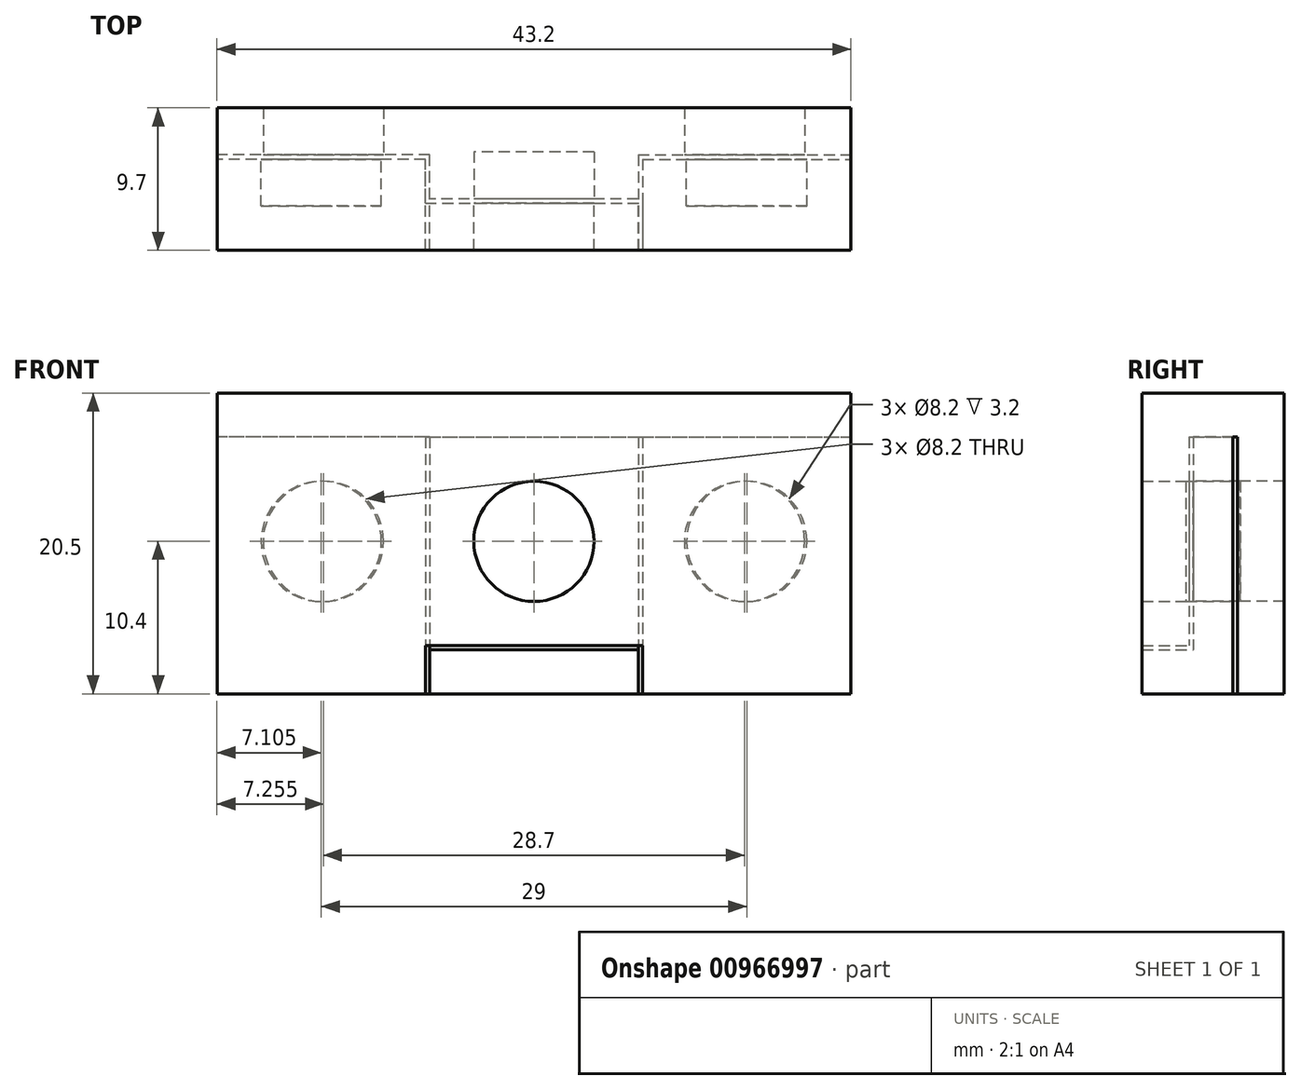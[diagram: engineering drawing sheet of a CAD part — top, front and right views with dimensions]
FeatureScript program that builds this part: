
annotation { "Feature Type Name" : "Feature", "Feature Type Description" : "" }
export const myFeature = defineFeature(function(context is Context, id is Id, definition is map)
    precondition{}
    {
        {
            var Q0;
            Q0=qCreatedBy(makeId("Top.planeOp"),FACE);
            var sketch = newSketch(context, id + "F0", { "sketchPlane" : qUnion([Q0])});
            skLineSegment(sketch, "E0.bottom", {"start": v(-40.9, 15.59) * mm, "end": v(2.3, 15.59) * mm});
            skLineSegment(sketch, "E0.top", {"start": v(-40.9, 25.29) * mm, "end": v(2.3, 25.29) * mm});
            skLineSegment(sketch, "E1", {"start": v(-26.7, 18.79) * mm, "end": v(-11.9, 18.79) * mm});
            skLineSegment(sketch, "E2", {"start": v(-26.7, 21.79) * mm, "end": v(-40.9, 21.79) * mm});
            skLineSegment(sketch, "E3", {"start": v(-11.9, 21.79) * mm, "end": v(2.3, 21.79) * mm});
            skLineSegment(sketch, "E4", {"start": v(-11.9, 21.79) * mm, "end": v(-11.9, 18.79) * mm});
            skLineSegment(sketch, "E5", {"start": v(-26.7, 18.79) * mm, "end": v(-26.7, 21.79) * mm});
            skLineSegment(sketch, "E6.0", {"start": v(-12.2, 22.09) * mm, "end": v(2.3, 22.09) * mm});
            skLineSegment(sketch, "E6.1", {"start": v(-26.4, 22.09) * mm, "end": v(-40.9, 22.09) * mm});
            skLineSegment(sketch, "E6.2", {"start": v(-26.4, 19.09) * mm, "end": v(-26.4, 22.09) * mm});
            skLineSegment(sketch, "E6.3", {"start": v(-26.4, 19.09) * mm, "end": v(-12.2, 19.09) * mm});
            skLineSegment(sketch, "E6.4", {"start": v(-12.2, 22.09) * mm, "end": v(-12.2, 19.09) * mm});
            skLineSegment(sketch, "E7", {"start": v(-40.9, 15.59) * mm, "end": v(-40.9, 21.79) * mm});
            skLineSegment(sketch, "E8", {"start": v(2.3, 15.59) * mm, "end": v(2.3, 21.79) * mm});
            skLineSegment(sketch, "E9", {"start": v(2.3, 22.09) * mm, "end": v(2.3, 25.29) * mm});
            skLineSegment(sketch, "E10", {"start": v(-40.9, 22.09) * mm, "end": v(-40.9, 25.29) * mm});
            skSolve(sketch);
        }
        {
            var Q0;
            Q0=makeQuery(id+"F0.imprint","IMPRINT",FACE,{"disambiguationData":[TD([[makeQuery(id+"F0.imprint","IMPRINT",EDGE,{"derivedFrom":sQuery(id+"F0.wireOp",EDGE,"E0.bottom")}),1.0]])]});
            extrude(context, id + "F1", {"entities" : qUnion([Q0]), "depth" : 14.2 * mm, "offsetDistance" : 25 * mm});
        }
        {
            var Q0;
            Q0=makeQuery(id+"F0.imprint","IMPRINT",FACE,{"disambiguationData":[TD([[makeQuery(id+"F0.imprint","IMPRINT",EDGE,{"derivedFrom":sQuery(id+"F0.wireOp",EDGE,"E0.top")}),-1.0]])]});
            extrude(context, id + "F2", {"entities" : qUnion([Q0]), "depth" : 14.2 * mm, "offsetDistance" : 25 * mm});
        }
        {
            var Q0;
            Q0=makeQuery(id+"F1.opExtrude","SWEPT_FACE",FACE,{"disambiguationData":[OSD([sQuery(id+"F0.wireOp",EDGE,"E2")])]});
            var sketch = newSketch(context, id + "F3", { "sketchPlane" : qUnion([Q0])});
            skCircle(sketch, "E11", {"center": v(33.8, 7.1) * mm, "radius": 4.1 * mm});
            skSolve(sketch);
        }
        {
            var Q0;
            Q0=makeQuery(id+"F1.opExtrude","SWEPT_FACE",FACE,{"disambiguationData":[OSD([sQuery(id+"F0.wireOp",EDGE,"E3")])]});
            var sketch = newSketch(context, id + "F4", { "sketchPlane" : qUnion([Q0])});
            skCircle(sketch, "E12", {"center": v(4.8, 7.1) * mm, "radius": 4.1 * mm});
            skSolve(sketch);
        }
        {
            var Q0;
            Q0=makeQuery(id+"F4.imprint","IMPRINT",FACE,{"disambiguationData":[TD([[makeQuery(id+"F4.imprint","IMPRINT",EDGE,{"derivedFrom":sQuery(id+"F4.wireOp",EDGE,"E12")}),1.0]])]});
            var Q1;
            Q1=makeQuery(id+"F3.imprint","IMPRINT",FACE,{"disambiguationData":[TD([[makeQuery(id+"F3.imprint","IMPRINT",EDGE,{"derivedFrom":sQuery(id+"F3.wireOp",EDGE,"E11")}),1.0]])]});
            extrude(context, id + "F5", {"entities" : qUnion([Q0, Q1]), "operationType" : NewBodyOperationType.REMOVE, "oppositeDirection" : true, "depth" : 3.2 * mm, "offsetDistance" : 25 * mm});
        }
        {
            var Q0;
            Q0=makeQuery(id+"F1.opExtrude","SWEPT_FACE",FACE,{"disambiguationData":[OSD([sQuery(id+"F0.wireOp",EDGE,"E1")])]});
            var sketch = newSketch(context, id + "F6", { "sketchPlane" : qUnion([Q0])});
            skCircle(sketch, "E13", {"center": v(19.3, 7.1) * mm, "radius": 4.1 * mm});
            skLineSegment(sketch, "E14", {"start": v(19.3, 14.2) * mm, "end": v(19.3, 0) * mm, "construction": true});
            skSolve(sketch);
        }
        {
            var Q0;
            Q0=makeQuery(id+"F6.imprint","IMPRINT",FACE,{"disambiguationData":[TD([[makeQuery(id+"F6.imprint","IMPRINT",EDGE,{"derivedFrom":sQuery(id+"F6.wireOp",EDGE,"E13")}),1.0]])]});
            extrude(context, id + "F7", {"entities" : qUnion([Q0]), "operationType" : NewBodyOperationType.REMOVE, "endBound" : BoundingType.THROUGH_ALL, "oppositeDirection" : true, "depth" : 25 * mm, "offsetDistance" : 25 * mm});
        }
        {
            var Q0;
            Q0=makeQuery(id+"F2.opExtrude","SWEPT_FACE",FACE,{"disambiguationData":[OSD([sQuery(id+"F0.wireOp",EDGE,"E6.1")])]});
            var sketch = newSketch(context, id + "F8", { "sketchPlane" : qUnion([Q0])});
            skCircle(sketch, "E15", {"center": v(-33.65, 7.1) * mm, "radius": 4.1 * mm});
            skLineSegment(sketch, "E16", {"start": v(-33.65, 0) * mm, "end": v(-33.65, 14.2) * mm, "construction": true});
            skSolve(sketch);
        }
        {
            var Q0;
            Q0=makeQuery(id+"F2.opExtrude","SWEPT_FACE",FACE,{"disambiguationData":[OSD([sQuery(id+"F0.wireOp",EDGE,"E6.0")])]});
            var sketch = newSketch(context, id + "F9", { "sketchPlane" : qUnion([Q0])});
            skCircle(sketch, "E17", {"center": v(-4.95, 7.1) * mm, "radius": 4.1 * mm});
            skLineSegment(sketch, "E18", {"start": v(-4.95, 0) * mm, "end": v(-4.95, 14.2) * mm, "construction": true});
            skSolve(sketch);
        }
        {
            var Q0;
            Q0=makeQuery(id+"F2.opExtrude","SWEPT_FACE",FACE,{"disambiguationData":[OSD([sQuery(id+"F0.wireOp",EDGE,"E6.3")])]});
            var sketch = newSketch(context, id + "F10", { "sketchPlane" : qUnion([Q0])});
            skCircle(sketch, "E19", {"center": v(-19.3, 7.1) * mm, "radius": 4.1 * mm});
            skLineSegment(sketch, "E20", {"start": v(-19.3, 0) * mm, "end": v(-19.3, 14.2) * mm, "construction": true});
            skSolve(sketch);
        }
        {
            var Q0;
            Q0=makeQuery(id+"F9.imprint","IMPRINT",FACE,{"disambiguationData":[TD([[makeQuery(id+"F9.imprint","IMPRINT",EDGE,{"derivedFrom":sQuery(id+"F9.wireOp",EDGE,"E17")}),1.0]])]});
            var Q1;
            Q1=makeQuery(id+"F8.imprint","IMPRINT",FACE,{"disambiguationData":[TD([[makeQuery(id+"F8.imprint","IMPRINT",EDGE,{"derivedFrom":sQuery(id+"F8.wireOp",EDGE,"E15")}),1.0]])]});
            extrude(context, id + "F11", {"entities" : qUnion([Q0, Q1]), "operationType" : NewBodyOperationType.REMOVE, "oppositeDirection" : true, "depth" : 3.2 * mm, "offsetDistance" : 25 * mm});
        }
        {
            var Q0;
            Q0=makeQuery(id+"F10.imprint","IMPRINT",FACE,{"disambiguationData":[TD([[makeQuery(id+"F10.imprint","IMPRINT",EDGE,{"derivedFrom":sQuery(id+"F10.wireOp",EDGE,"E19")}),1.0]])]});
            extrude(context, id + "F12", {"entities" : qUnion([Q0]), "operationType" : NewBodyOperationType.REMOVE, "oppositeDirection" : true, "depth" : 3.2 * mm, "offsetDistance" : 25 * mm});
        }
        {
            var Q0;
            Q0=makeQuery(id+"F1.opExtrude","SWEPT_FACE",FACE,{"disambiguationData":[OSD([sQuery(id+"F0.wireOp",EDGE,"E0.bottom")])]});
            var sketch = newSketch(context, id + "F13", { "sketchPlane" : qUnion([Q0])});
            skLineSegment(sketch, "E21.bottom", {"start": v(-40.9, 14.2) * mm, "end": v(2.3, 14.2) * mm});
            skLineSegment(sketch, "E21.top", {"start": v(-40.9, 17.2) * mm, "end": v(2.3, 17.2) * mm});
            skLineSegment(sketch, "E21.left", {"start": v(-40.9, 14.2) * mm, "end": v(-40.9, 17.2) * mm});
            skLineSegment(sketch, "E21.right", {"start": v(2.3, 14.2) * mm, "end": v(2.3, 17.2) * mm});
            skSolve(sketch);
        }
        {
            var Q0;
            Q0=makeQuery(id+"F13.imprint","IMPRINT",FACE,{"disambiguationData":[TD([[makeQuery(id+"F13.imprint","IMPRINT",EDGE,{"derivedFrom":sQuery(id+"F13.wireOp",EDGE,"E21.bottom")}),1.0]])]});
            var Q1;
            Q1=makeQuery(id+"F2.opExtrude","SWEPT_FACE",FACE,{"disambiguationData":[OSD([sQuery(id+"F0.wireOp",EDGE,"E0.top")])]});
            extrude(context, id + "F14", {"entities" : qUnion([Q0]), "operationType" : NewBodyOperationType.ADD, "endBound" : BoundingType.UP_TO_SURFACE, "oppositeDirection" : true, "depth" : 25 * mm, "endBoundEntityFace" : qUnion([Q1]), "offsetDistance" : 25 * mm});
        }
        {
            var Q0;
            Q0=makeQuery(id+"F1.opExtrude","CAP_FACE",FACE,{"disambiguationData":[OSD([sQuery(id+"F0.wireOp",EDGE,"E0.bottom"),sQuery(id+"F0.wireOp",EDGE,"E1"),sQuery(id+"F0.wireOp",EDGE,"E2"),sQuery(id+"F0.wireOp",EDGE,"E3"),sQuery(id+"F0.wireOp",EDGE,"E4"),sQuery(id+"F0.wireOp",EDGE,"E5"),sQuery(id+"F0.wireOp",EDGE,"E7"),sQuery(id+"F0.wireOp",EDGE,"E8")])],"isStart":true});
            var sketch = newSketch(context, id + "F15", { "sketchPlane" : qUnion([Q0])});
            skLineSegment(sketch, "E22.bottom", {"start": v(-26.7, -21.79) * mm, "end": v(-40.9, -21.79) * mm});
            skLineSegment(sketch, "E22.top", {"start": v(-26.7, -15.59) * mm, "end": v(-40.9, -15.59) * mm});
            skLineSegment(sketch, "E22.left", {"start": v(-26.7, -21.79) * mm, "end": v(-26.7, -15.59) * mm});
            skLineSegment(sketch, "E22.right", {"start": v(-40.9, -21.79) * mm, "end": v(-40.9, -15.59) * mm});
            skLineSegment(sketch, "E23", {"start": v(-19.3, -18.79) * mm, "end": v(-19.3, -15.59) * mm, "construction": true});
            skLineSegment(sketch, "E24.MirrorCS", {"start": v(-11.9, -15.59) * mm, "end": v(2.3, -15.59) * mm});
            skLineSegment(sketch, "E25.MirrorCS", {"start": v(-11.9, -21.79) * mm, "end": v(2.3, -21.79) * mm});
            skLineSegment(sketch, "E26.MirrorCS", {"start": v(-11.9, -21.79) * mm, "end": v(-11.9, -15.59) * mm});
            skLineSegment(sketch, "E27.MirrorCS", {"start": v(2.3, -21.79) * mm, "end": v(2.3, -15.59) * mm});
            skSolve(sketch);
        }
        {
            var Q0;
            Q0=makeQuery(id+"F15.imprint","IMPRINT",FACE,{"disambiguationData":[TD([[makeQuery(id+"F15.imprint","IMPRINT",EDGE,{"derivedFrom":sQuery(id+"F15.wireOp",EDGE,"E22.bottom")}),-1.0]])]});
            var Q1;
            Q1=makeQuery(id+"F15.imprint","IMPRINT",FACE,{"disambiguationData":[TD([[makeQuery(id+"F15.imprint","IMPRINT",EDGE,{"derivedFrom":sQuery(id+"F15.wireOp",EDGE,"E24.MirrorCS")}),-1.0]])]});
            extrude(context, id + "F16", {"entities" : qUnion([Q0, Q1]), "operationType" : NewBodyOperationType.ADD, "depth" : 3.3 * mm, "offsetDistance" : 25 * mm});
        }
        {
            var Q0;
            Q0=makeQuery(id+"F2.opExtrude","CAP_FACE",FACE,{"disambiguationData":[OSD([sQuery(id+"F0.wireOp",EDGE,"E0.top"),sQuery(id+"F0.wireOp",EDGE,"E6.0"),sQuery(id+"F0.wireOp",EDGE,"E6.1"),sQuery(id+"F0.wireOp",EDGE,"E6.2"),sQuery(id+"F0.wireOp",EDGE,"E6.3"),sQuery(id+"F0.wireOp",EDGE,"E6.4"),sQuery(id+"F0.wireOp",EDGE,"E9"),sQuery(id+"F0.wireOp",EDGE,"E10")])],"isStart":true});
            var Q1;
            Q1=makeQuery(id+"F16.opExtrude","CAP_FACE",FACE,{"disambiguationData":[OSD([sQuery(id+"F15.wireOp",EDGE,"E24.MirrorCS"),sQuery(id+"F15.wireOp",EDGE,"E25.MirrorCS"),sQuery(id+"F15.wireOp",EDGE,"E26.MirrorCS"),sQuery(id+"F15.wireOp",EDGE,"E27.MirrorCS")])],"isStart":false});
            extrude(context, id + "F17", {"entities" : qUnion([Q0]), "operationType" : NewBodyOperationType.ADD, "endBound" : BoundingType.UP_TO_SURFACE, "depth" : 3 * mm, "endBoundEntityFace" : qUnion([Q1]), "offsetDistance" : 25 * mm});
        }
        {
            var Q0;
            {var subQ0=sQuery(id+"F0.wireOp",EDGE,"E6.3");Q0=makeQuery(id+"F17.boolean.opBoolean","MERGE",FACE,{"derivedFrom":[makeQuery(id+"F2.opExtrude","SWEPT_FACE",FACE,{"disambiguationData":[OSD([subQ0])]}),makeQuery(id+"F17.opExtrude","SWEPT_FACE",FACE,{"disambiguationData":[OSD([subQ0])]})]});}
            var sketch = newSketch(context, id + "F18", { "sketchPlane" : qUnion([Q0])});
            skLineSegment(sketch, "E28.bottom", {"start": v(-12.2, -3.3) * mm, "end": v(-26.4, -3.3) * mm});
            skLineSegment(sketch, "E28.top", {"start": v(-12.2, -0.3) * mm, "end": v(-26.4, -0.3) * mm});
            skLineSegment(sketch, "E28.left", {"start": v(-12.2, -3.3) * mm, "end": v(-12.2, -0.3) * mm});
            skLineSegment(sketch, "E28.right", {"start": v(-26.4, -3.3) * mm, "end": v(-26.4, -0.3) * mm});
            skSolve(sketch);
        }
        {
            var Q0;
            Q0=makeQuery(id+"F18.imprint","IMPRINT",FACE,{"disambiguationData":[TD([[makeQuery(id+"F18.imprint","IMPRINT",EDGE,{"derivedFrom":sQuery(id+"F18.wireOp",EDGE,"E28.bottom")}),1.0]])]});
            var Q1;
            Q1=makeQuery(id+"F14.boolean.opBoolean","MERGE",FACE,{"derivedFrom":[makeQuery(id+"F1.opExtrude","SWEPT_FACE",FACE,{"disambiguationData":[OSD([sQuery(id+"F0.wireOp",EDGE,"E0.bottom")])]}),makeQuery(id+"F14.opExtrude","CAP_FACE",FACE,{"disambiguationData":[OSD([sQuery(id+"F13.wireOp",EDGE,"E21.bottom"),sQuery(id+"F13.wireOp",EDGE,"E21.top"),sQuery(id+"F13.wireOp",EDGE,"E21.left"),sQuery(id+"F13.wireOp",EDGE,"E21.right")])],"isStart":true})]});
            extrude(context, id + "F19", {"entities" : qUnion([Q0]), "operationType" : NewBodyOperationType.ADD, "endBound" : BoundingType.UP_TO_SURFACE, "depth" : 25 * mm, "endBoundEntityFace" : qUnion([Q1]), "offsetDistance" : 25 * mm});
        }
    });
